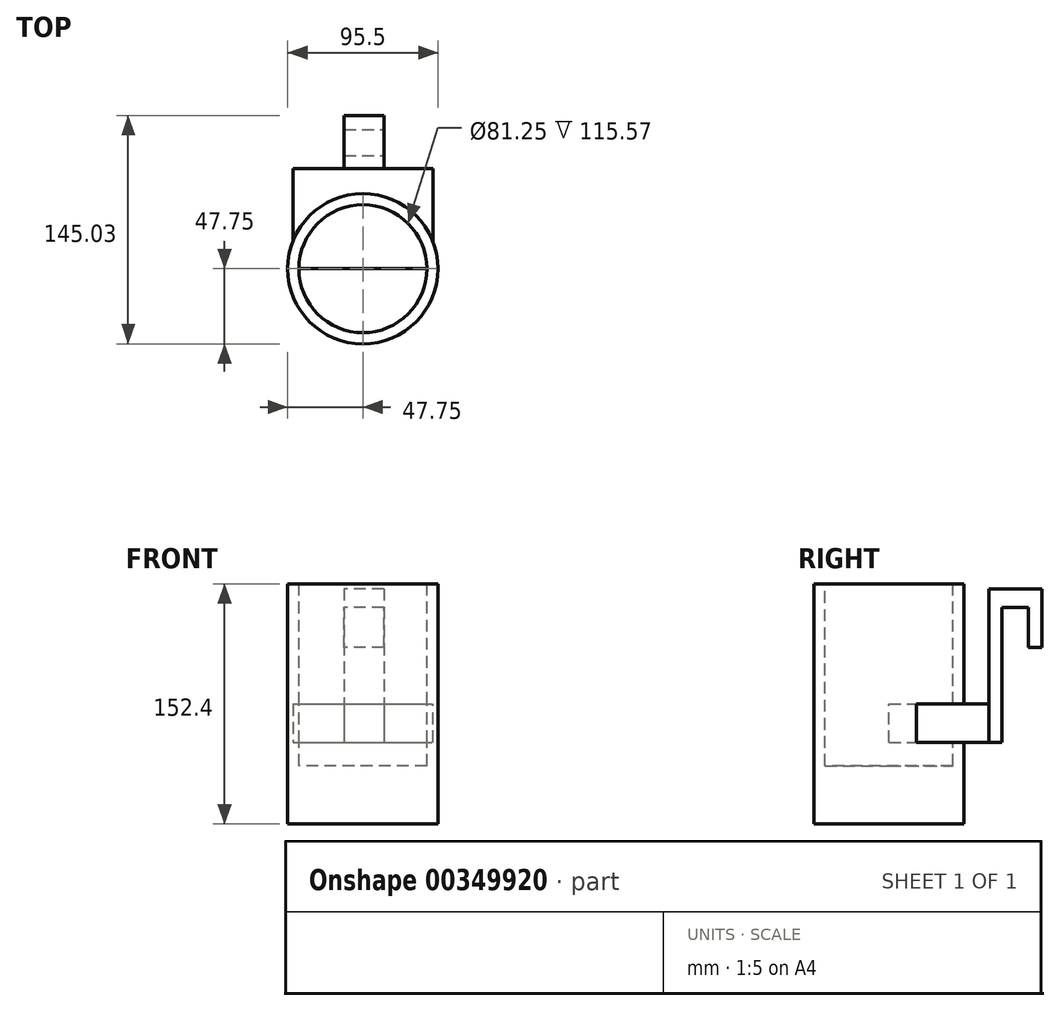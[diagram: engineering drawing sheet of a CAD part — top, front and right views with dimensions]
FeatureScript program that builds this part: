
annotation { "Feature Type Name" : "Feature", "Feature Type Description" : "" }
export const myFeature = defineFeature(function(context is Context, id is Id, definition is map)
    precondition{}
    {
        {
            var Q0;
            Q0=qCreatedBy(makeId("Top.planeOp"),FACE);
            var sketch = newSketch(context, id + "F0", { "sketchPlane" : qUnion([Q0])});
            skCircle(sketch, "E0", {"center": v(0, 0) * mm, "radius": 47.75 * mm});
            skSolve(sketch);
        }
        {
            var Q0;
            Q0 = qSketchRegion(id + "F0", true);
            extrude(context, id + "F1", {"entities" : qUnion([Q0]), "depth" : 152.4 * mm, "offsetDistance" : 25.4 * mm});
        }
        {
            var Q0;
            Q0=makeQuery(id+"F1.opExtrude","CAP_FACE",FACE,{"disambiguationData":[OSD([sQuery(id+"F0.wireOp",EDGE,"E0")])],"isStart":false});
            var sketch = newSketch(context, id + "F2", { "sketchPlane" : qUnion([Q0])});
            skCircle(sketch, "E1", {"center": v(0, 0) * mm, "radius": 40.63 * mm});
            skSolve(sketch);
        }
        {
            var Q0;
            Q0 = qSketchRegion(id + "F2", true);
            extrude(context, id + "F3", {"entities" : qUnion([Q0]), "operationType" : NewBodyOperationType.REMOVE, "oppositeDirection" : true, "depth" : 115.57 * mm, "offsetDistance" : 25.4 * mm});
        }
        {
            var Q0;
            Q0=qCreatedBy(makeId("Front.planeOp"),FACE);
            var sketch = newSketch(context, id + "F4", { "sketchPlane" : qUnion([Q0])});
            skLineSegment(sketch, "E2.bottom", {"start": v(-44.44, 51.86) * mm, "end": v(44.44, 51.86) * mm});
            skLineSegment(sketch, "E2.top", {"start": v(-44.44, 76.23) * mm, "end": v(44.44, 76.23) * mm});
            skLineSegment(sketch, "E2.left", {"start": v(-44.44, 51.86) * mm, "end": v(-44.44, 76.23) * mm});
            skLineSegment(sketch, "E2.right", {"start": v(44.44, 51.86) * mm, "end": v(44.44, 76.23) * mm});
            skPoint(sketch, "E2.middle", {"position": v(0, 64.04) * mm});
            skSolve(sketch);
        }
        {
            var Q0;
            Q0 = qSketchRegion(id + "F4", true);
            extrude(context, id + "F5", {"entities" : qUnion([Q0]), "operationType" : NewBodyOperationType.ADD, "oppositeDirection" : true, "depth" : 63.5 * mm, "offsetDistance" : 25.4 * mm});
        }
        {
            var Q0;
            Q0=makeQuery(id+"F5.opExtrude","CAP_FACE",FACE,{"disambiguationData":[OSD([sQuery(id+"F4.wireOp",EDGE,"E2.bottom"),sQuery(id+"F4.wireOp",EDGE,"E2.top"),sQuery(id+"F4.wireOp",EDGE,"E2.left"),sQuery(id+"F4.wireOp",EDGE,"E2.right")])],"isStart":false});
            var sketch = newSketch(context, id + "F6", { "sketchPlane" : qUnion([Q0])});
            skLineSegment(sketch, "E3.bottom", {"start": v(-13.3, 149.32) * mm, "end": v(11.96, 149.32) * mm});
            skLineSegment(sketch, "E3.top", {"start": v(-13.3, 51.86) * mm, "end": v(11.96, 51.86) * mm});
            skLineSegment(sketch, "E3.left", {"start": v(-13.3, 149.32) * mm, "end": v(-13.3, 51.86) * mm});
            skLineSegment(sketch, "E3.right", {"start": v(11.96, 149.32) * mm, "end": v(11.96, 51.86) * mm});
            skSolve(sketch);
        }
        {
            var Q0;
            Q0 = qSketchRegion(id + "F6", true);
            extrude(context, id + "F7", {"entities" : qUnion([Q0]), "operationType" : NewBodyOperationType.ADD, "depth" : 8.38 * mm, "offsetDistance" : 25.4 * mm});
        }
        {
            var Q0;
            Q0=makeQuery(id+"F7.opExtrude","CAP_FACE",FACE,{"disambiguationData":[OSD([sQuery(id+"F6.wireOp",EDGE,"E3.bottom"),sQuery(id+"F6.wireOp",EDGE,"E3.top"),sQuery(id+"F6.wireOp",EDGE,"E3.left"),sQuery(id+"F6.wireOp",EDGE,"E3.right")])],"isStart":false});
            var sketch = newSketch(context, id + "F8", { "sketchPlane" : qUnion([Q0])});
            skLineSegment(sketch, "E4.bottom", {"start": v(-13.3, 149.32) * mm, "end": v(11.96, 149.32) * mm});
            skLineSegment(sketch, "E4.top", {"start": v(-13.3, 137.59) * mm, "end": v(11.96, 137.59) * mm});
            skLineSegment(sketch, "E4.left", {"start": v(-13.3, 149.32) * mm, "end": v(-13.3, 137.59) * mm});
            skLineSegment(sketch, "E4.right", {"start": v(11.96, 149.32) * mm, "end": v(11.96, 137.59) * mm});
            skSolve(sketch);
        }
        {
            var Q0;
            Q0 = qSketchRegion(id + "F8", true);
            extrude(context, id + "F9", {"entities" : qUnion([Q0]), "operationType" : NewBodyOperationType.ADD, "depth" : 25.4 * mm, "offsetDistance" : 25.4 * mm});
        }
        {
            var Q0;
            Q0=makeQuery(id+"F9.opExtrude","SWEPT_FACE",FACE,{"disambiguationData":[OSD([sQuery(id+"F8.wireOp",EDGE,"E4.top")])]});
            var sketch = newSketch(context, id + "F10", { "sketchPlane" : qUnion([Q0])});
            skLineSegment(sketch, "E5.bottom", {"start": v(-11.96, -88.44) * mm, "end": v(13.3, -88.44) * mm});
            skLineSegment(sketch, "E5.top", {"start": v(-11.96, -97.28) * mm, "end": v(13.3, -97.28) * mm});
            skLineSegment(sketch, "E5.left", {"start": v(-11.96, -88.44) * mm, "end": v(-11.96, -97.28) * mm});
            skLineSegment(sketch, "E5.right", {"start": v(13.3, -88.44) * mm, "end": v(13.3, -97.28) * mm});
            skSolve(sketch);
        }
        {
            var Q0;
            Q0 = qSketchRegion(id + "F10", true);
            extrude(context, id + "F11", {"entities" : qUnion([Q0]), "operationType" : NewBodyOperationType.ADD, "depth" : 25.4 * mm, "offsetDistance" : 25.4 * mm});
        }
    });
